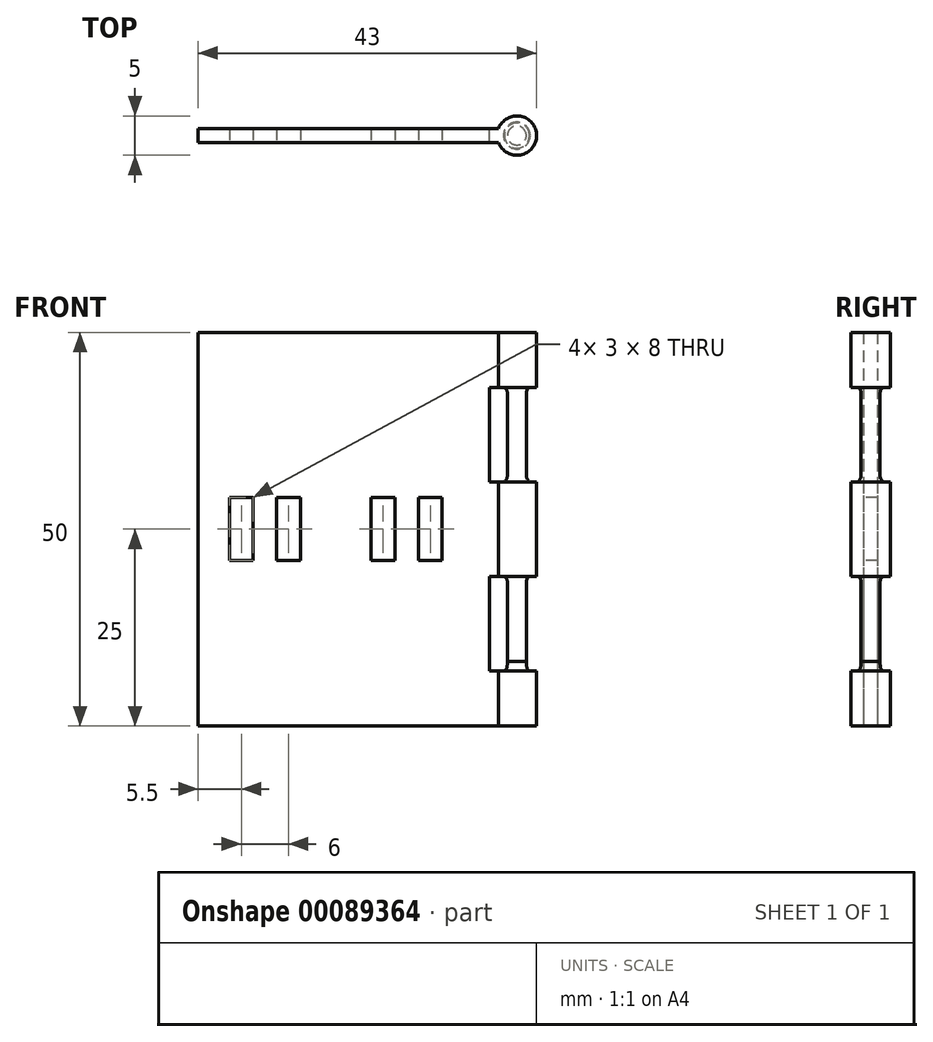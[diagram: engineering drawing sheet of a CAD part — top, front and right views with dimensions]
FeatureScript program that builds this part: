
annotation { "Feature Type Name" : "Feature", "Feature Type Description" : "" }
export const myFeature = defineFeature(function(context is Context, id is Id, definition is map)
    precondition{}
    {
        {
            var Q0;
            Q0=qCreatedBy(makeId("Top.planeOp"),FACE);
            var sketch = newSketch(context, id + "F0", { "sketchPlane" : qUnion([Q0])});
            skLineSegment(sketch, "E0.bottom", {"start": v(-38, 0.9) * mm, "end": v(0, 0.9) * mm});
            skLineSegment(sketch, "E0.top", {"start": v(-38, -0.9) * mm, "end": v(0, -0.9) * mm});
            skLineSegment(sketch, "E0.left", {"start": v(-38, 0.9) * mm, "end": v(-38, -0.9) * mm});
            skLineSegment(sketch, "E0.right", {"start": v(0, 0.9) * mm, "end": v(0, -0.9) * mm});
            skPoint(sketch, "E1", {"position": v(0, 0) * mm});
            skCircle(sketch, "E2", {"center": v(2.5, 0) * mm, "radius": 2.5 * mm, "construction": true});
            skLineSegment(sketch, "E3", {"start": v(0, 0.9) * mm, "end": v(0.17, 0.9) * mm});
            skLineSegment(sketch, "E4", {"start": v(0, -0.9) * mm, "end": v(0.17, -0.9) * mm});
            skArc(sketch, "E5", {"start": v(0.17, -0.9) * mm, "mid": v(5, 0) * mm, "end": v(0.17, 0.9) * mm});
            skSolve(sketch);
        }
        {
            var Q0;
            Q0 = qSketchRegion(id + "F0", true);
            extrude(context, id + "F1", {"entities" : qUnion([Q0]), "depth" : 50 * mm});
        }
        {
            var Q0;
            Q0=qCreatedBy(makeId("Right.planeOp"),FACE);
            var sketch = newSketch(context, id + "F2", { "sketchPlane" : qUnion([Q0])});
            skLineSegment(sketch, "E6.bottom", {"start": v(-13.75, 43) * mm, "end": v(19.34, 43) * mm});
            skLineSegment(sketch, "E6.top", {"start": v(-13.75, 31) * mm, "end": v(19.34, 31) * mm});
            skLineSegment(sketch, "E6.left", {"start": v(-13.75, 43) * mm, "end": v(-13.75, 31) * mm});
            skLineSegment(sketch, "E6.right", {"start": v(19.34, 43) * mm, "end": v(19.34, 31) * mm});
            skLineSegment(sketch, "E7.bottom", {"start": v(-14.45, 19) * mm, "end": v(21.9, 19) * mm});
            skLineSegment(sketch, "E7.top", {"start": v(-14.45, 7) * mm, "end": v(21.9, 7) * mm});
            skLineSegment(sketch, "E7.left", {"start": v(-14.45, 19) * mm, "end": v(-14.45, 7) * mm});
            skLineSegment(sketch, "E7.right", {"start": v(21.9, 19) * mm, "end": v(21.9, 7) * mm});
            skSolve(sketch);
        }
        {
            var Q0;
            Q0 = qSketchRegion(id + "F2", true);
            extrude(context, id + "F3", {"entities" : qUnion([Q0]), "operationType" : NewBodyOperationType.REMOVE, "depth" : 25 * mm});
        }
        {
            var Q0;
            Q0=qCreatedBy(makeId("Right.planeOp"),FACE);
            var sketch = newSketch(context, id + "F4", { "sketchPlane" : qUnion([Q0])});
            skLineSegment(sketch, "E8.bottom", {"start": v(-17.01, 43) * mm, "end": v(16.08, 43) * mm});
            skLineSegment(sketch, "E8.top", {"start": v(-17.01, 31) * mm, "end": v(16.08, 31) * mm});
            skLineSegment(sketch, "E8.left", {"start": v(-17.01, 43) * mm, "end": v(-17.01, 31) * mm});
            skLineSegment(sketch, "E8.right", {"start": v(16.08, 43) * mm, "end": v(16.08, 31) * mm});
            skLineSegment(sketch, "E9.bottom", {"start": v(-17.71, 19) * mm, "end": v(18.64, 19) * mm});
            skLineSegment(sketch, "E9.top", {"start": v(-17.71, 7) * mm, "end": v(18.64, 7) * mm});
            skLineSegment(sketch, "E9.left", {"start": v(-17.71, 19) * mm, "end": v(-17.71, 7) * mm});
            skLineSegment(sketch, "E9.right", {"start": v(18.64, 19) * mm, "end": v(18.64, 7) * mm});
            skSolve(sketch);
        }
        {
            var Q0;
            Q0=makeQuery(id+"F1.opExtrude","SWEPT_FACE",FACE,{"disambiguationData":[OSD([sQuery(id+"F0.wireOp",EDGE,"E0.top"),sQuery(id+"F0.wireOp",EDGE,"E4")])]});
            var sketch = newSketch(context, id + "F5", { "sketchPlane" : qUnion([Q0])});
            skLineSegment(sketch, "E10.bottom", {"start": v(-34, 29) * mm, "end": v(-31, 29) * mm});
            skLineSegment(sketch, "E10.top", {"start": v(-34, 21) * mm, "end": v(-31, 21) * mm});
            skLineSegment(sketch, "E10.left", {"start": v(-34, 29) * mm, "end": v(-34, 21) * mm});
            skLineSegment(sketch, "E10.right", {"start": v(-31, 29) * mm, "end": v(-31, 21) * mm});
            skLineSegment(sketch, "E11.1.0.0", {"start": v(-25, 29) * mm, "end": v(-25, 21) * mm});
            skLineSegment(sketch, "E11.1.0.1", {"start": v(-28, 29) * mm, "end": v(-28, 21) * mm});
            skLineSegment(sketch, "E11.1.0.2", {"start": v(-28, 21) * mm, "end": v(-25, 21) * mm});
            skLineSegment(sketch, "E11.1.0.3", {"start": v(-28, 29) * mm, "end": v(-25, 29) * mm});
            skLineSegment(sketch, "E11.direction1", {"start": v(-31, 21) * mm, "end": v(-25, 21) * mm, "construction": true});
            skLineSegment(sketch, "E12.1.0.0", {"start": v(-13, 29) * mm, "end": v(-13, 21) * mm});
            skLineSegment(sketch, "E12.1.0.1", {"start": v(-16, 29) * mm, "end": v(-16, 21) * mm});
            skLineSegment(sketch, "E12.1.0.2", {"start": v(-10, 29) * mm, "end": v(-10, 21) * mm});
            skLineSegment(sketch, "E12.1.0.3", {"start": v(-7, 29) * mm, "end": v(-7, 21) * mm});
            skLineSegment(sketch, "E12.1.0.4", {"start": v(-16, 29) * mm, "end": v(-13, 29) * mm});
            skLineSegment(sketch, "E12.1.0.5", {"start": v(-16, 21) * mm, "end": v(-13, 21) * mm});
            skLineSegment(sketch, "E12.1.0.6", {"start": v(-10, 29) * mm, "end": v(-7, 29) * mm});
            skLineSegment(sketch, "E12.1.0.7", {"start": v(-10, 21) * mm, "end": v(-7, 21) * mm});
            skLineSegment(sketch, "E12.1.0.8", {"start": v(-13, 21) * mm, "end": v(-7, 21) * mm, "construction": true});
            skLineSegment(sketch, "E12.direction1", {"start": v(-31, 21) * mm, "end": v(-13, 21) * mm, "construction": true});
            skLineSegment(sketch, "E12.direction2", {"start": v(-31, 21) * mm, "end": v(-31, -27) * mm, "construction": true});
            skSolve(sketch);
        }
        {
            var Q0;
            Q0 = qSketchRegion(id + "F5", true);
            extrude(context, id + "F6", {"entities" : qUnion([Q0]), "operationType" : NewBodyOperationType.REMOVE, "endBound" : BoundingType.UP_TO_NEXT, "oppositeDirection" : true, "depth" : 25 * mm});
        }
        {
            var Q0;
            Q0=makeQuery(id+"F3.boolean.opBoolean","COPY",FACE,{"derivedFrom":makeQuery(id+"F3.opExtrude","SWEPT_FACE",FACE,{"disambiguationData":[OSD([sQuery(id+"F2.wireOp",EDGE,"E6.top")])]})});
            var sketch = newSketch(context, id + "F7", { "sketchPlane" : qUnion([Q0])});
            skCircle(sketch, "E13", {"center": v(2.5, 0) * mm, "radius": 2.5 * mm, "construction": true});
            skPoint(sketch, "E13.first.point", {"position": v(0.8, 1.84) * mm});
            skPoint(sketch, "E13.second.point", {"position": v(5, 0) * mm});
            skPoint(sketch, "E13.third.point", {"position": v(1.04, -2.03) * mm});
            skCircle(sketch, "E14", {"center": v(2.5, 0) * mm, "radius": 1.5 * mm});
            skSolve(sketch);
        }
        {
            var Q0;
            Q0=qCreatedBy(makeId("Front.planeOp"),FACE);
            var sketch = newSketch(context, id + "F8", { "sketchPlane" : qUnion([Q0])});
            skLineSegment(sketch, "E15.bottom", {"start": v(2.5, 31) * mm, "end": v(4.1, 31) * mm, "construction": true});
            skLineSegment(sketch, "E15.top", {"start": v(2.5, 32.2) * mm, "end": v(4.1, 32.2) * mm, "construction": true});
            skLineSegment(sketch, "E15.left", {"start": v(2.5, 31) * mm, "end": v(2.5, 32.2) * mm, "construction": true});
            skLineSegment(sketch, "E15.right", {"start": v(4.1, 31) * mm, "end": v(4.1, 32.2) * mm, "construction": true});
            skLineSegment(sketch, "E16", {"start": v(5, 31) * mm, "end": v(0, 31) * mm, "construction": true});
            skPoint(sketch, "E17", {"position": v(2.5, 31) * mm});
            skPoint(sketch, "E18", {"position": v(3.7, 32.2) * mm});
            skFitSpline(sketch, "E19", {"points": [v(3.7, 32.2) * mm, v(4.1, 31) * mm], "startDerivative": vector(0.01, -2.09) * mm, "endDerivative": vector(1.1, -1.22) * mm});
            skLineSegment(sketch, "E20", {"start": v(2.5, 31) * mm, "end": v(2.5, 32.2) * mm});
            skLineSegment(sketch, "E21", {"start": v(2.5, 32.2) * mm, "end": v(3.7, 32.2) * mm});
            skLineSegment(sketch, "E22", {"start": v(4.1, 31) * mm, "end": v(2.5, 31) * mm});
            skLineSegment(sketch, "E23", {"start": v(5, 7) * mm, "end": v(0, 7) * mm, "construction": true});
            skPoint(sketch, "E24", {"position": v(2.5, 7) * mm});
            skLineSegment(sketch, "E25.bottom", {"start": v(2.5, 7) * mm, "end": v(4.2, 7) * mm});
            skLineSegment(sketch, "E25.top", {"start": v(2.5, 8.2) * mm, "end": v(4.2, 8.2) * mm, "construction": true});
            skLineSegment(sketch, "E25.left", {"start": v(2.5, 8.2) * mm, "end": v(2.5, 7) * mm});
            skLineSegment(sketch, "E25.right", {"start": v(4.2, 8.2) * mm, "end": v(4.2, 7) * mm, "construction": true});
            skLineSegment(sketch, "E26", {"start": v(2.5, 8.2) * mm, "end": v(3.7, 8.2) * mm});
            skFitSpline(sketch, "E27", {"points": [v(4.2, 7) * mm, v(3.7, 8.2) * mm], "startDerivative": vector(-1.47, 0) * mm, "endDerivative": vector(-0.08, 1.6) * mm});
            skSolve(sketch);
        }
        {
            var Q0;
            Q0 = qSketchRegion(id + "F8", true);
            var Q1;
            Q1=sQuery(id+"F8.wireOp",EDGE,"E20");
            revolve(context, id + "F9", {"operationType" : NewBodyOperationType.ADD, "entities" : qUnion([Q0]), "axis" : qUnion([Q1]), "revolveType" : RevolveType.FULL});
        }
        {
            var Q0;
            Q0=makeQuery(id+"F1.opExtrude","CAP_FACE",FACE,{"disambiguationData":[OSD([sQuery(id+"F0.wireOp",EDGE,"E0.bottom"),sQuery(id+"F0.wireOp",EDGE,"E0.top"),sQuery(id+"F0.wireOp",EDGE,"E0.left"),sQuery(id+"F0.wireOp",EDGE,"E3"),sQuery(id+"F0.wireOp",EDGE,"E4"),sQuery(id+"F0.wireOp",EDGE,"E5")])],"isStart":true});
            var sketch = newSketch(context, id + "F10", { "sketchPlane" : qUnion([Q0])});
            skCircle(sketch, "E28", {"center": v(2.5, 0) * mm, "radius": 1.2 * mm});
            skPoint(sketch, "E28.first.point", {"position": v(1.5, 0.65) * mm});
            skPoint(sketch, "E28.second.point", {"position": v(3.58, 0.52) * mm});
            skPoint(sketch, "E28.third.point", {"position": v(2.53, 1.2) * mm});
            skSolve(sketch);
        }
        {
            var Q0;
            Q0 = qSketchRegion(id + "F10", true);
            var Q1;
            Q1=makeQuery(id+"F3.boolean.opBoolean","COPY",FACE,{"derivedFrom":makeQuery(id+"F3.opExtrude","SWEPT_FACE",FACE,{"disambiguationData":[OSD([sQuery(id+"F2.wireOp",EDGE,"E6.bottom")])]})});
            extrude(context, id + "F11", {"entities" : qUnion([Q0]), "operationType" : NewBodyOperationType.ADD, "endBound" : BoundingType.UP_TO_SURFACE, "oppositeDirection" : true, "endBoundEntityFace" : qUnion([Q1]), "depth" : 17 * mm});
        }
        {
            var Q0;
            Q0=qCreatedBy(makeId("Front.planeOp"),FACE);
            var sketch = newSketch(context, id + "F12", { "sketchPlane" : qUnion([Q0])});
            skLineSegment(sketch, "E29", {"start": v(5, 43) * mm, "end": v(0, 43) * mm, "construction": true});
            skPoint(sketch, "E30", {"position": v(2.5, 43) * mm});
            skLineSegment(sketch, "E31.bottom", {"start": v(2.5, 43) * mm, "end": v(4.2, 43) * mm});
            skLineSegment(sketch, "E31.top", {"start": v(2.5, 41.8) * mm, "end": v(4.2, 41.8) * mm, "construction": true});
            skLineSegment(sketch, "E31.left", {"start": v(2.5, 43) * mm, "end": v(2.5, 41.8) * mm});
            skLineSegment(sketch, "E31.right", {"start": v(4.2, 43) * mm, "end": v(4.2, 41.8) * mm, "construction": true});
            skLineSegment(sketch, "E32", {"start": v(2.5, 41.8) * mm, "end": v(3.7, 41.8) * mm});
            skFitSpline(sketch, "E33", {"points": [v(4.2, 43) * mm, v(3.7, 41.8) * mm], "startDerivative": vector(-1.5, -0.36) * mm, "endDerivative": vector(0, -1.91) * mm});
            skLineSegment(sketch, "E34", {"start": v(5, 19) * mm, "end": v(0, 19) * mm, "construction": true});
            skPoint(sketch, "E35", {"position": v(2.5, 19) * mm});
            skLineSegment(sketch, "E36.bottom", {"start": v(2.5, 19) * mm, "end": v(4.2, 19) * mm});
            skLineSegment(sketch, "E36.top", {"start": v(2.5, 17.8) * mm, "end": v(4.2, 17.8) * mm, "construction": true});
            skLineSegment(sketch, "E36.left", {"start": v(2.5, 19) * mm, "end": v(2.5, 17.8) * mm});
            skLineSegment(sketch, "E36.right", {"start": v(4.2, 19) * mm, "end": v(4.2, 17.8) * mm, "construction": true});
            skLineSegment(sketch, "E37", {"start": v(2.5, 17.8) * mm, "end": v(3.7, 17.8) * mm});
            skFitSpline(sketch, "E38", {"points": [v(4.2, 19) * mm, v(3.7, 17.8) * mm], "startDerivative": vector(-1.5, -0.36) * mm, "endDerivative": vector(0, -1.91) * mm});
            skSolve(sketch);
        }
        {
            var Q0;
            Q0 = qSketchRegion(id + "F12", true);
            var Q1;
            Q1=sQuery(id+"F12.wireOp",EDGE,"E31.left");
            revolve(context, id + "F13", {"operationType" : NewBodyOperationType.ADD, "entities" : qUnion([Q0]), "axis" : qUnion([Q1]), "revolveType" : RevolveType.FULL});
        }
        {
            var Q0;
            Q0 = qSketchRegion(id + "F4", true);
            extrude(context, id + "F14", {"entities" : qUnion([Q0]), "operationType" : NewBodyOperationType.REMOVE, "oppositeDirection" : true, "depth" : 1 * mm});
        }
    });
